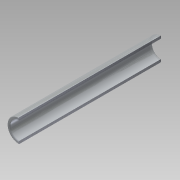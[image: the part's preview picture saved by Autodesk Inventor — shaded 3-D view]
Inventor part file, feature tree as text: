
AUTODESK INVENTOR PART (.ipt)
format: ipt  version: 2014 (Build 180170000, 170)  size: 113,664 bytes
history: native  units: mm
features: fillet x3, other x1, extrude x1, sketch x1
ambient origin geometry x8: Origin, YZ Plane, XZ Plane, XY Plane, X Axis, Y Axis, Z Axis, Center Point
bodies: Body1 (feature_tree)
feature tree (6):
  other  "CrossSection1"
  extrude  "Extrusion2"  Depth=10.0mm
  fillet  "Fillet1"  Radius=80.0mm
  fillet  "Fillet2"  Radius=0.3mm
  fillet  "Fillet3"  Radius=0.3mm
  sketch  "Sketch3"  dims[d4=13.0mm d6=10.0mm d7=80.0mm d8=0.0mm d9=0.3mm d10=0.3mm d11=0.3mm d12=0.5mm d13=2.0mm d14=0.0mm d15=20.0mm]
